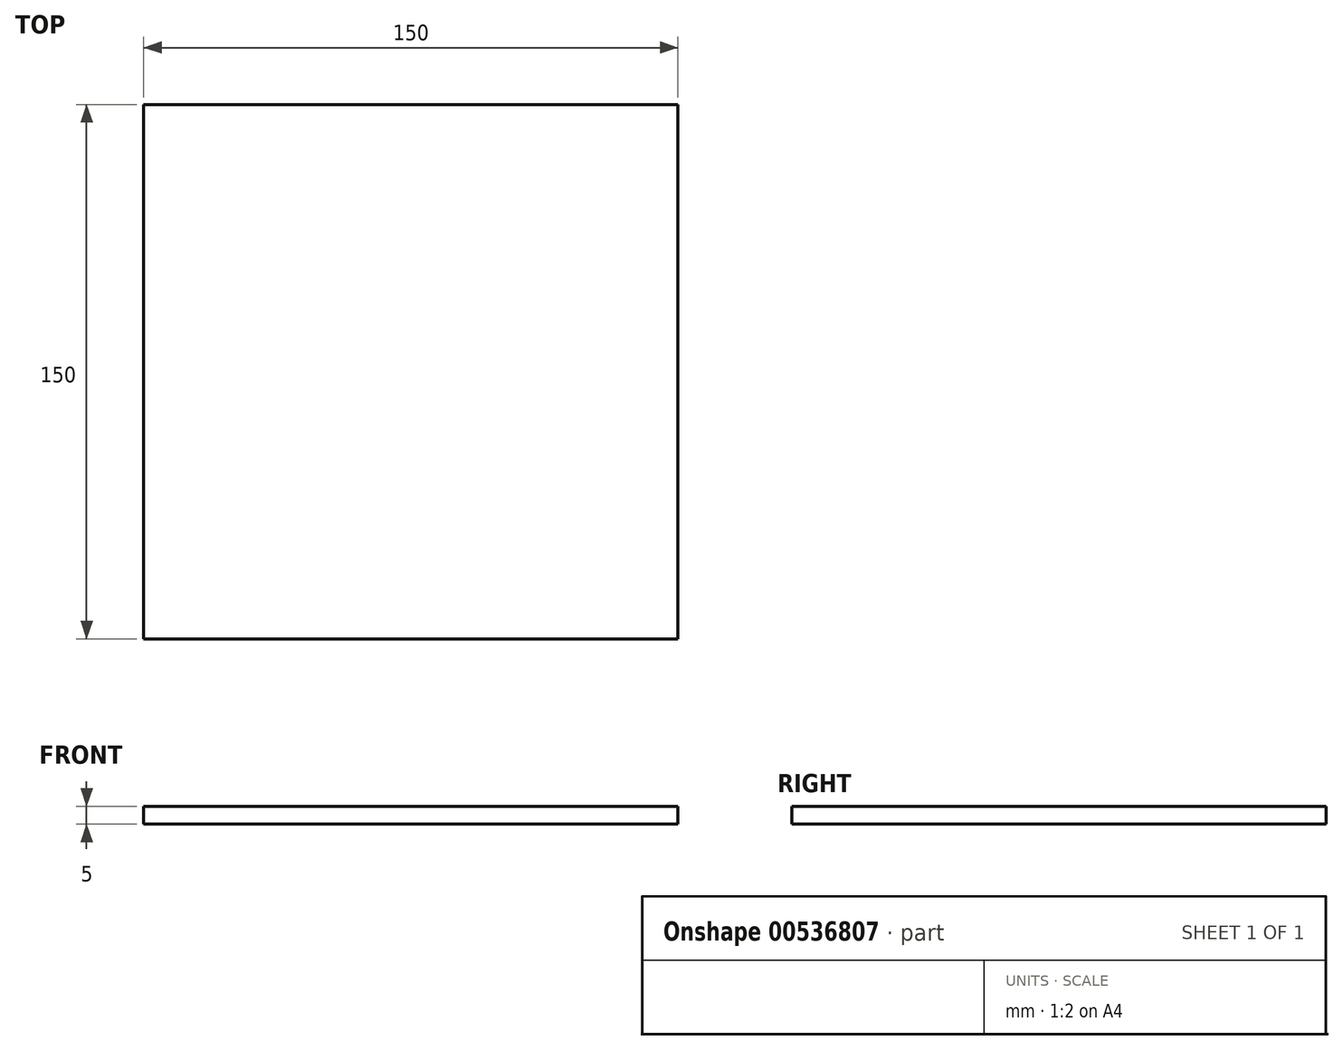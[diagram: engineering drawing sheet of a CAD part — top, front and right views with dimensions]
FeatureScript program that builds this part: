
annotation { "Feature Type Name" : "Feature", "Feature Type Description" : "" }
export const myFeature = defineFeature(function(context is Context, id is Id, definition is map)
    precondition{}
    {
        {
            var Q0;
            Q0=qCreatedBy(makeId("Top.planeOp"),FACE);
            var sketch = newSketch(context, id + "F0", { "sketchPlane" : qUnion([Q0])});
            skLineSegment(sketch, "E0.bottom", {"start": v(75, -75) * mm, "end": v(-75, -75) * mm});
            skLineSegment(sketch, "E0.top", {"start": v(75, 75) * mm, "end": v(-75, 75) * mm});
            skLineSegment(sketch, "E0.left", {"start": v(75, -75) * mm, "end": v(75, 75) * mm});
            skLineSegment(sketch, "E0.right", {"start": v(-75, -75) * mm, "end": v(-75, 75) * mm});
            skPoint(sketch, "E0.middle", {"position": v(0, 0) * mm});
            skSolve(sketch);
        }
        {
            var Q0;
            Q0=makeQuery(id+"F0.imprint","IMPRINT",FACE,{"disambiguationData":[TD([[makeQuery(id+"F0.imprint","IMPRINT",EDGE,{"derivedFrom":sQuery(id+"F0.wireOp",EDGE,"E0.bottom")}),-1.0]])]});
            extrude(context, id + "F1", {"entities" : qUnion([Q0]), "depth" : 5 * mm, "offsetDistance" : 25 * mm});
        }
    });
